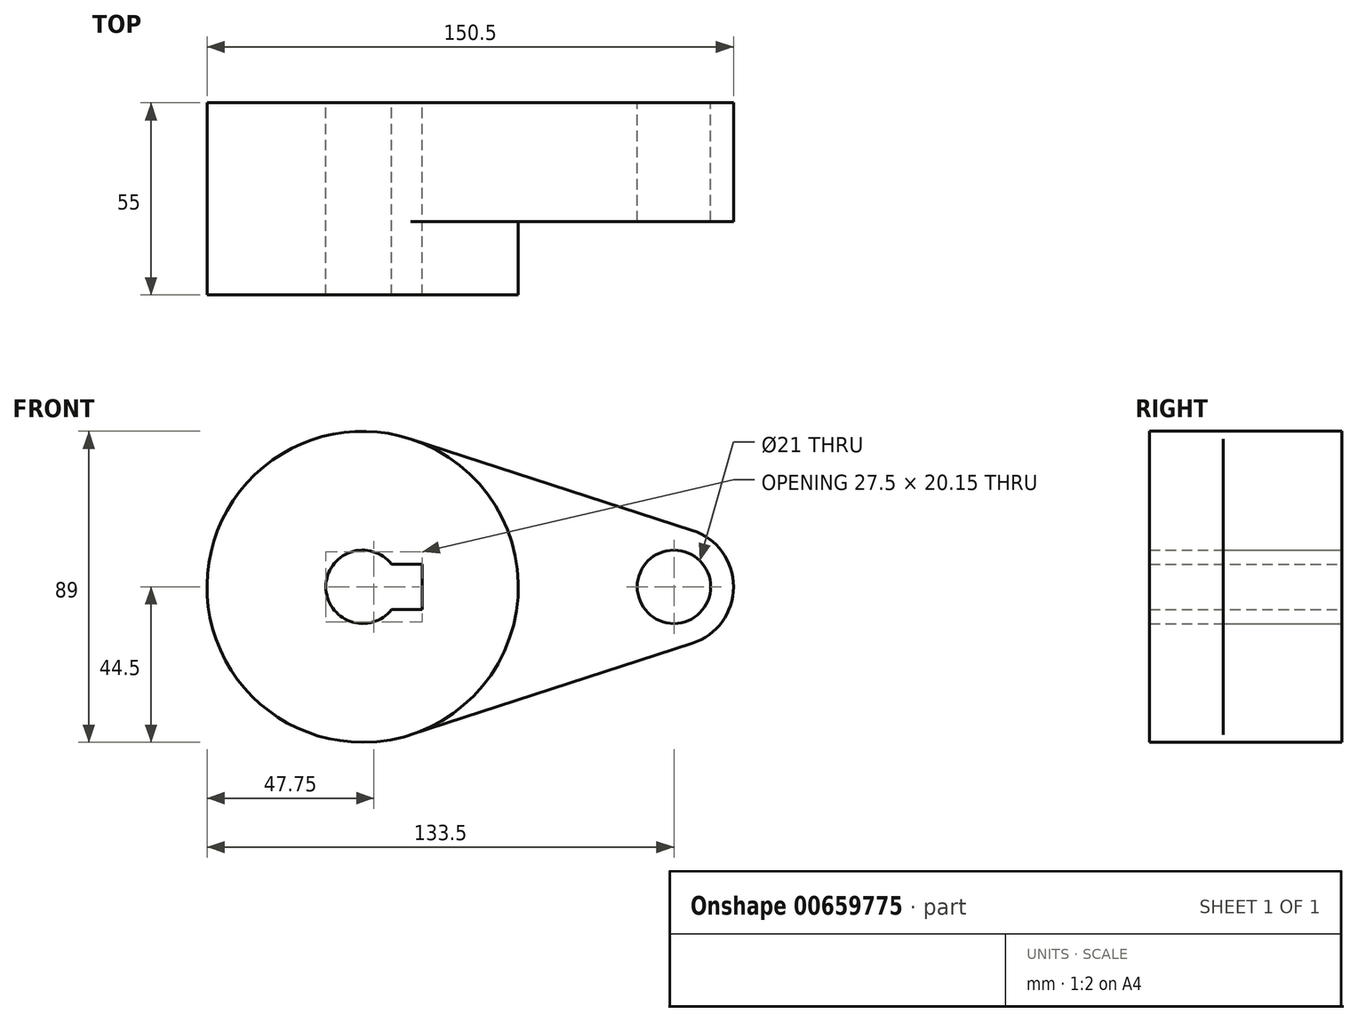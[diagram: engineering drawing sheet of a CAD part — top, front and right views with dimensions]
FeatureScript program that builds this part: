
annotation { "Feature Type Name" : "Feature", "Feature Type Description" : "" }
export const myFeature = defineFeature(function(context is Context, id is Id, definition is map)
    precondition{}
    {
        {
            var Q0;
            Q0=qCreatedBy(makeId("Front.planeOp"),FACE);
            var sketch = newSketch(context, id + "F0", { "sketchPlane" : qUnion([Q0])});
            skCircle(sketch, "E0", {"center": v(0, 0) * mm, "radius": 44.5 * mm});
            skCircle(sketch, "E1", {"center": v(89, 0) * mm, "radius": 17 * mm});
            skLineSegment(sketch, "E2", {"start": v(13.75, 42.32) * mm, "end": v(94.25, 16.17) * mm});
            skLineSegment(sketch, "E3", {"start": v(13.75, -42.32) * mm, "end": v(94.25, -16.17) * mm});
            skCircle(sketch, "E4", {"center": v(0, 0) * mm, "radius": 10.5 * mm});
            skCircle(sketch, "E5", {"center": v(89, 0) * mm, "radius": 10.5 * mm});
            skLineSegment(sketch, "E6.bottom", {"start": v(17, -6.5) * mm, "end": v(-17, -6.5) * mm});
            skLineSegment(sketch, "E6.top", {"start": v(17, 6.5) * mm, "end": v(-17, 6.5) * mm});
            skLineSegment(sketch, "E6.left", {"start": v(17, -6.5) * mm, "end": v(17, 6.5) * mm});
            skLineSegment(sketch, "E6.right", {"start": v(-17, -6.5) * mm, "end": v(-17, 6.5) * mm});
            skSolve(sketch);
        }
        {
            var Q0;
            Q0=makeQuery(id+"F0.imprint","IMPRINT",FACE,{"disambiguationData":[TD([[makeQuery(id+"F0.imprint","IMPRINT",EDGE,{"derivedFrom":sQuery(id+"F0.wireOp",EDGE,"E5")}),-1.0]])]});
            var Q1;
            {var subQ0=sQuery(id+"F0.wireOp",EDGE,"E2");Q1=makeQuery(id+"F0.imprint","IMPRINT",FACE,{"disambiguationData":[TD([[makeQuery(id+"F0.imprint","IMPRINT",EDGE,{"derivedFrom":subQ0}),-1.0]])]});}
            var Q2;
            {var subQ7=sQuery(id+"F0.wireOp",EDGE,"E6.left");Q2=makeQuery(id+"F0.imprint","IMPRINT",FACE,{"disambiguationData":[TD([[makeQuery(id+"F0.imprint","IMPRINT",EDGE,{"derivedFrom":subQ7}),-1.0]])]});}
            var Q3;
            {var subQ5=sQuery(id+"F0.wireOp",EDGE,"E6.right");Q3=makeQuery(id+"F0.imprint","IMPRINT",FACE,{"disambiguationData":[TD([[makeQuery(id+"F0.imprint","IMPRINT",EDGE,{"derivedFrom":subQ5}),-1.0]])]});}
            extrude(context, id + "F1", {"entities" : qUnion([Q0, Q1, Q2, Q3]), "depth" : 34 * mm, "offsetDistance" : 25 * mm});
        }
        {
            var Q0;
            {var subQ7=sQuery(id+"F0.wireOp",EDGE,"E6.left");Q0=makeQuery(id+"F0.imprint","IMPRINT",FACE,{"disambiguationData":[TD([[makeQuery(id+"F0.imprint","IMPRINT",EDGE,{"derivedFrom":subQ7}),-1.0]])]});}
            var Q1;
            {var subQ5=sQuery(id+"F0.wireOp",EDGE,"E6.right");Q1=makeQuery(id+"F0.imprint","IMPRINT",FACE,{"disambiguationData":[TD([[makeQuery(id+"F0.imprint","IMPRINT",EDGE,{"derivedFrom":subQ5}),-1.0]])]});}
            extrude(context, id + "F2", {"entities" : qUnion([Q0, Q1]), "operationType" : NewBodyOperationType.ADD, "depth" : 55 * mm, "offsetDistance" : 25 * mm});
        }
    });
